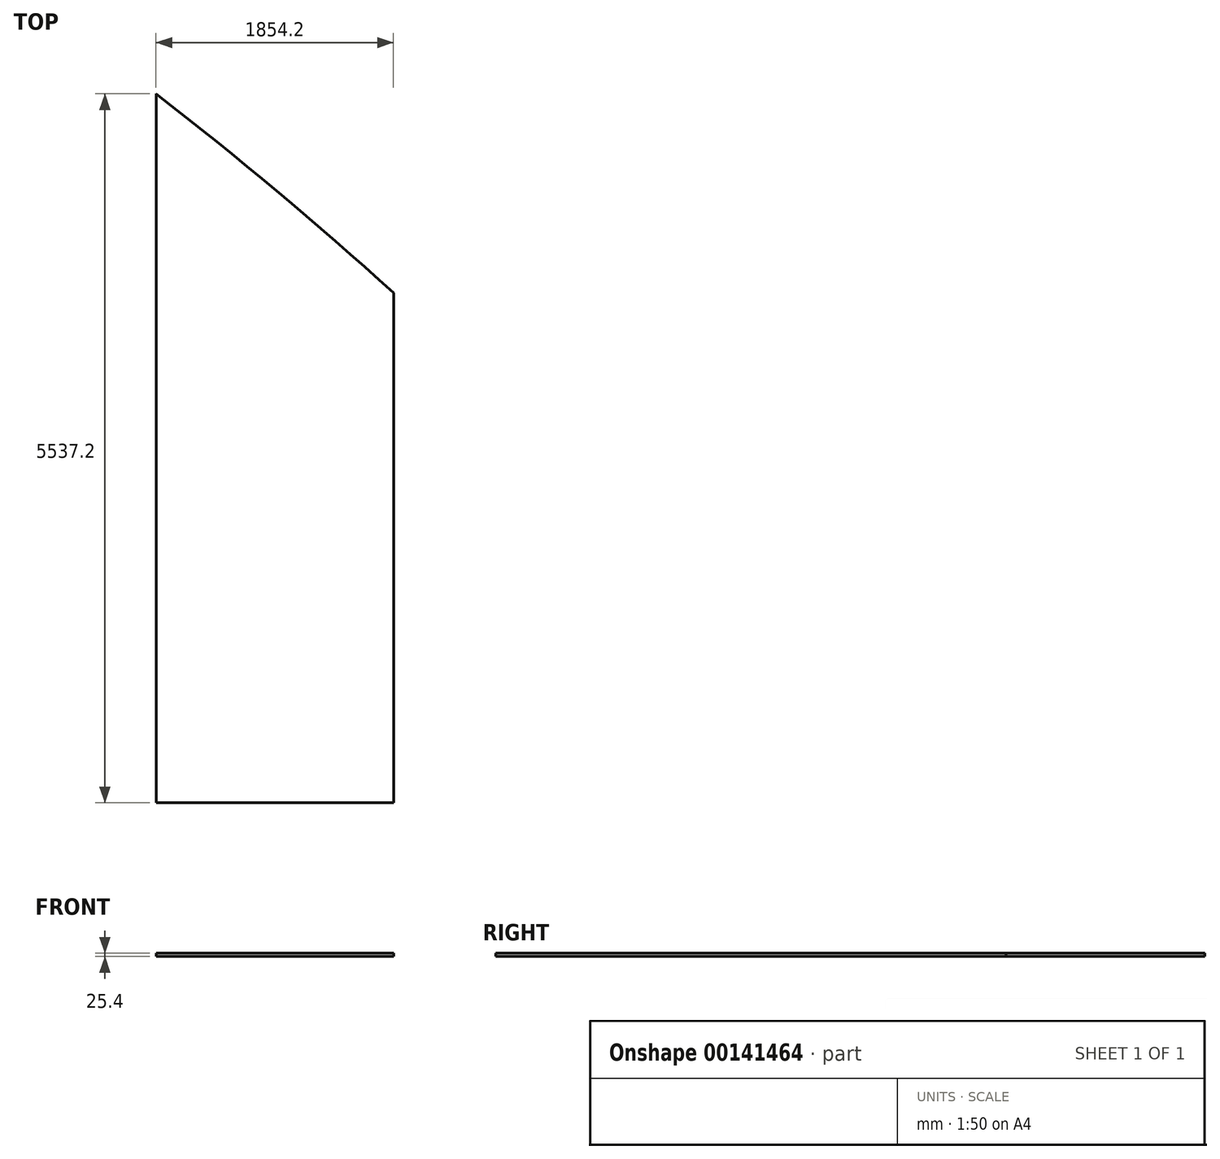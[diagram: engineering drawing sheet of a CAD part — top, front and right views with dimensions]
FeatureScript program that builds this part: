
annotation { "Feature Type Name" : "Feature", "Feature Type Description" : "" }
export const myFeature = defineFeature(function(context is Context, id is Id, definition is map)
    precondition{}
    {
        {
            var Q0;
            Q0=qCreatedBy(makeId("Top.planeOp"),FACE);
            var sketch = newSketch(context, id + "F0", { "sketchPlane" : qUnion([Q0])});
            skLineSegment(sketch, "E0", {"start": v(-949.59, -1416.96) * mm, "end": v(904.61, -1416.96) * mm});
            skLineSegment(sketch, "E1", {"start": v(-949.59, -1416.96) * mm, "end": v(-949.59, 4120.24) * mm});
            skLineSegment(sketch, "E2", {"start": v(904.61, -1416.96) * mm, "end": v(904.61, 2566.01) * mm});
            skLineSegment(sketch, "E3", {"start": v(-22.49, -1416.96) * mm, "end": v(-22.49, 3373.22) * mm});
            skArc(sketch, "E4", {"start": v(904.61, 2566.01) * mm, "mid": v(-7.67, 3360.8) * mm, "end": v(-949.59, 4120.24) * mm});
            skSolve(sketch);
        }
        {
            var Q0;
            {var subQ0=sQuery(id+"F0.wireOp",EDGE,"E1");Q0=makeQuery(id+"F0.imprint","IMPRINT",FACE,{"disambiguationData":[TD([[makeQuery(id+"F0.imprint","IMPRINT",EDGE,{"derivedFrom":subQ0}),-1.0]])]});}
            var Q1;
            {var subQ0=sQuery(id+"F0.wireOp",EDGE,"E2");Q1=makeQuery(id+"F0.imprint","IMPRINT",FACE,{"disambiguationData":[TD([[makeQuery(id+"F0.imprint","IMPRINT",EDGE,{"derivedFrom":subQ0}),1.0]])]});}
            extrude(context, id + "F1", {"entities" : qUnion([Q0, Q1]), "depth" : 25.4 * mm});
        }
    });
